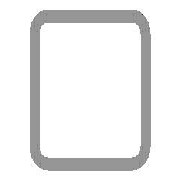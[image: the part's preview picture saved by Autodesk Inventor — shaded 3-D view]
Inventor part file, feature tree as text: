
AUTODESK INVENTOR PART (.ipt)
format: ipt  version: 2024.3 (Build 283343000, 343)  size: 141,312 bytes
history: native  units: mm (DEFAULTED — no unit token found)
features: other x4, plane x2, split x1, sketch x1
ambient origin geometry x8: Origin, YZ Plane, XZ Plane, XY Plane, X Axis, Y Axis, Z Axis, Center Point
bodies: Solid1 (feature_tree), Body (feature_tree)
feature tree (8):
  parser-record x1  (decoder bookkeeping rows leaked as tree rows — omitted from the tree; the rows remain in map.json)
  other  "Driven Length"
  other  "Start Plane"
  other  "End Plane"
  plane  "Work Plane4"
  split  "Split1"
  sketch  "Sketch3"  dims[d3=90.0mm d4=0.0mm d7=4.0mm d9=20.0mm d11=20.0mm d12=2.0mm d13=-0.0mm d14=90.0mm d15=10.0mm d16=10.0mm d17=90.0deg d18=90.0mm]
  plane  "Work Plane3"
